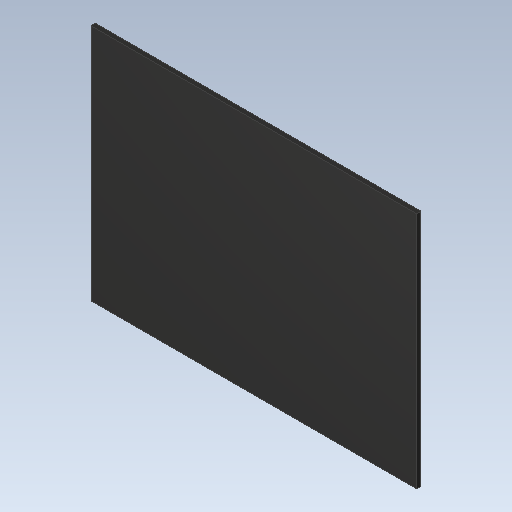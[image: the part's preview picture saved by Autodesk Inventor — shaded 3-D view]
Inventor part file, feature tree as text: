
AUTODESK INVENTOR PART (.ipt)
format: ipt  version: 2020 (Build 240168000, 168)  size: 86,528 bytes
history: imported  units: in
note: dims shown in document units (in); Inventor stores cm internally (conversion verified against a paired STEP export)
features: imported_body x1
ambient origin geometry x8: Origin, YZ Plane, XZ Plane, XY Plane, X Axis, Y Axis, Z Axis, Center Point
bodies: Solid1 (imported_parasolid), Body1 (imported_parasolid)
feature tree (1):
  imported_body  NMx_Import_Brep_tag  [imported B-rep: ~6 faces, bbox_mm=[7.45, 5.45, 0.1]]
